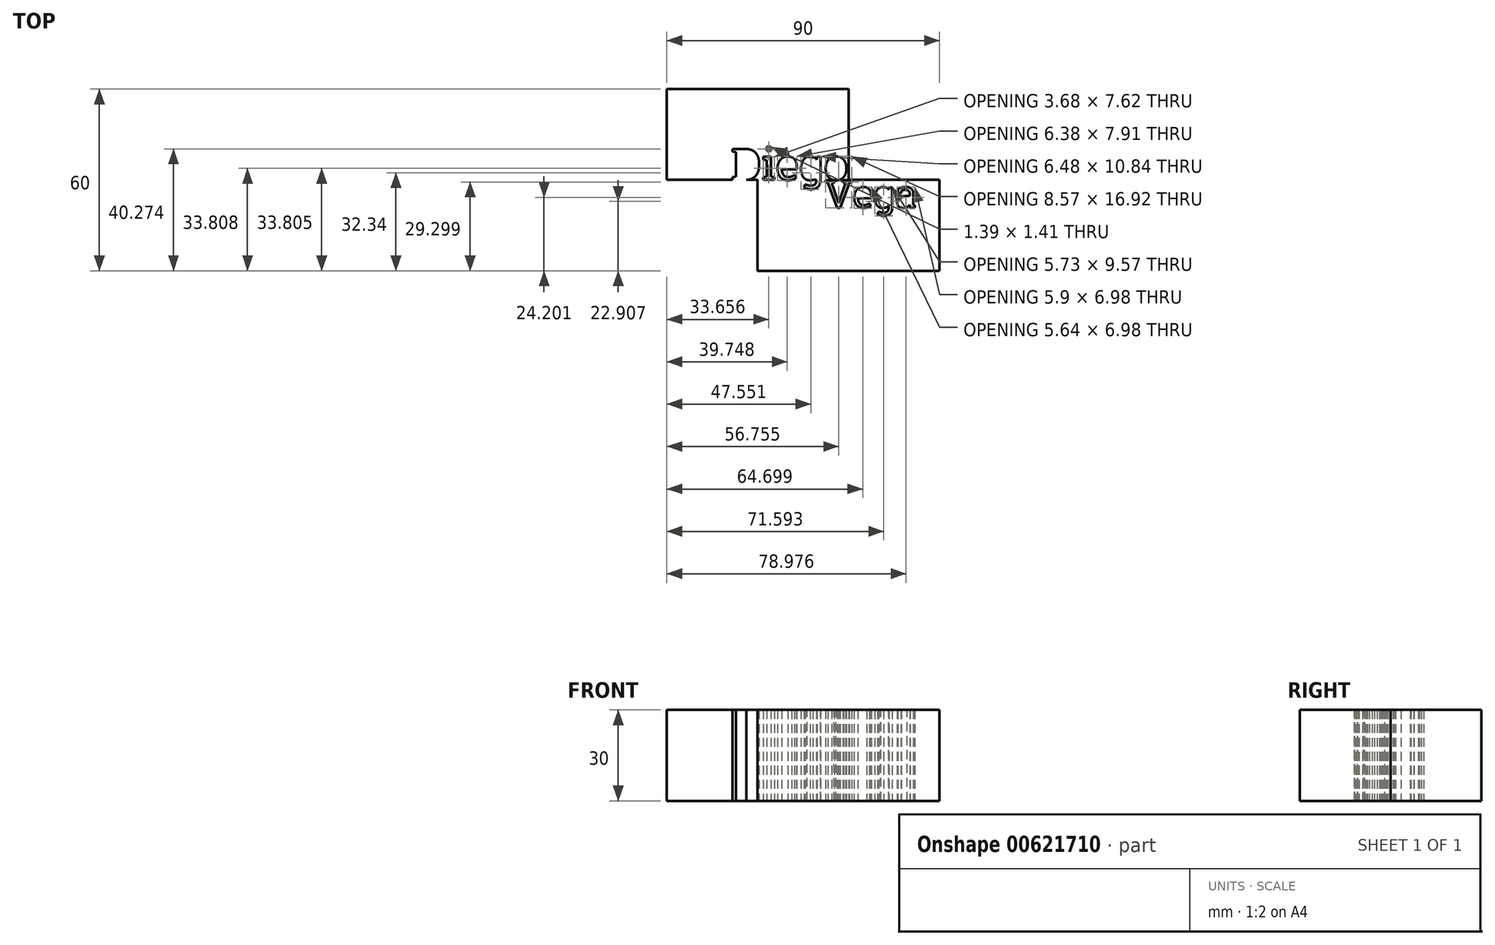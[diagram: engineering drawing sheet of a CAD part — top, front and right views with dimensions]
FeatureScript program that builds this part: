
annotation { "Feature Type Name" : "Feature", "Feature Type Description" : "" }
export const myFeature = defineFeature(function(context is Context, id is Id, definition is map)
    precondition{}
    {
        {
            var Q0;
            Q0=qCreatedBy(makeId("Top.planeOp"),FACE);
            var sketch = newSketch(context, id + "F0", { "sketchPlane" : qUnion([Q0])});
            skLineSegment(sketch, "E0.bottom", {"start": v(-52.18, 24.43) * mm, "end": v(7.82, 24.43) * mm});
            skLineSegment(sketch, "E0.top", {"start": v(-52.18, -5.57) * mm, "end": v(7.82, -5.57) * mm});
            skLineSegment(sketch, "E0.left", {"start": v(-52.18, 24.43) * mm, "end": v(-52.18, -5.57) * mm});
            skLineSegment(sketch, "E0.right", {"start": v(7.82, 24.43) * mm, "end": v(7.82, -5.57) * mm});
            skLineSegment(sketch, "E1.bottom", {"start": v(-22.18, -5.57) * mm, "end": v(37.82, -5.57) * mm});
            skLineSegment(sketch, "E1.top", {"start": v(-22.18, -35.57) * mm, "end": v(37.82, -35.57) * mm});
            skLineSegment(sketch, "E1.left", {"start": v(-22.18, -5.57) * mm, "end": v(-22.18, -35.57) * mm});
            skLineSegment(sketch, "E1.right", {"start": v(37.82, -5.57) * mm, "end": v(37.82, -35.57) * mm});
            skText(sketch, "E2", { "text": "Diego", "fontName": "RobotoSlab-Regular.ttf"});
            skText(sketch, "E3", { "text": "Vega", "fontName": "RobotoSlab-Regular.ttf"});
            const initialGuessF0  = {"E2": [-0.03098, -0.00557, 1, 0, 0.01038], "E3": [0, -0.01473, 1, 0, 0.00917]};
            skSetInitialGuess(sketch, initialGuessF0);
            skSolve(sketch);
        }
        {
            var Q0;
            Q0=makeQuery(id+"F0.imprint","IMPRINT",FACE,{"disambiguationData":[TD([[makeQuery(id+"F0.imprint","IMPRINT",EDGE,{"derivedFrom":sQuery(id+"F0.wireOp",EDGE,"E0.bottom")}),-1.0]])]});
            var Q1;
            Q1=makeQuery(id+"F0.imprint","IMPRINT",FACE,{"disambiguationData":[TD([[makeQuery(id+"F0.imprint","IMPRINT",EDGE,{"derivedFrom":sQuery(id+"F0.wireOp",EDGE,"E1.top")}),1.0]])]});
            extrude(context, id + "F1", {"entities" : qUnion([Q0, Q1]), "depth" : 30 * mm, "offsetDistance" : 25 * mm});
        }
    });
